# Revit family: Sensor Wall Mounted Spout
name_source: partatom
category: Generic Models
units: mm (PartAtom-declared; Revit-internal decimal feet)

## family parameters
Always vertical = Yes
Can host rebar = No
Cut with Voids When Loaded = No
Maintain Annotation Orientation = No
OmniClass Number = 23.31.11.00
Part Type = Normal
Room Calculation Point = No
Round Connector Dimension = Use Diameter
Shared = No
Work Plane-Based = No

## types (1)
- Sensor Wall Mounted Spout
    Category = Sensor
    Default Elevation = 0 mm  [stored 0 ft]
    Description = Sensor Wall Mounted Spout
    Keywords = Wall Mounted Spout, Sensor, Spout Tip Sensor
    Manufacturer = ABI Interiors Pty Ltd
    Model = Brushed Brass(15759), Brushed Copper(15760), Brushed Gunmetal(15761), Stainless Steel(15863), Matte Black(15862)
    Part Number = Brushed Brass(15759), Brushed Copper(15760), Brushed Gunmetal(15761), Stainless Steel(15863), Matte Black(15862)
    QR Link = https://abi.guide
    Spec Image = https://cdn.bfldr.com
    Title = Sensor Wall Mounted Spout
    URL = https://www.abiinteriors.com.au

note: [stored X ft] marks values corroborated as IEEE doubles in the binary element streams (Revit-internal decimal feet)

## geometry (parser evidence)
native form markers: Sweep x3
no freeform markers — native parametric forms only
